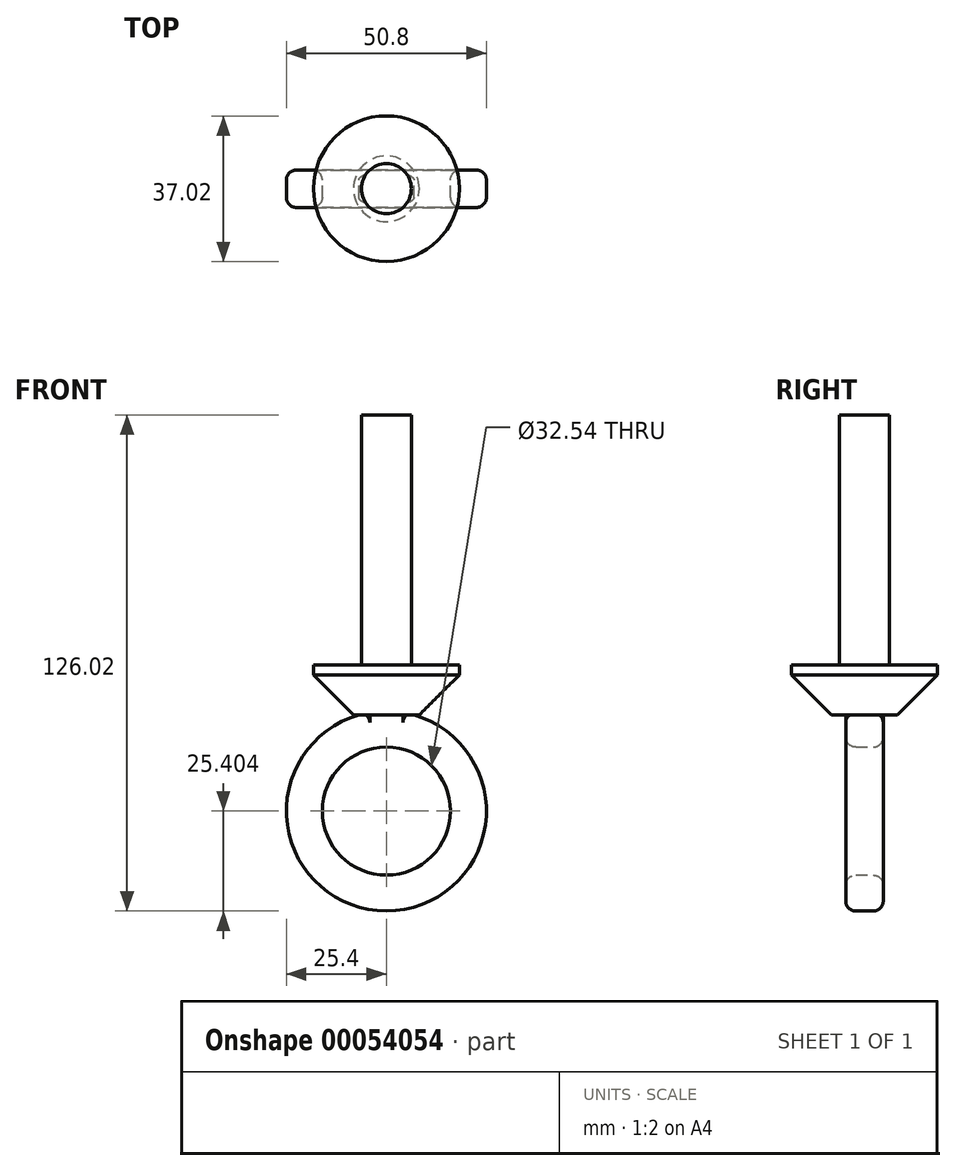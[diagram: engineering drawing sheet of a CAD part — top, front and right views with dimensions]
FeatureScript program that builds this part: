
annotation { "Feature Type Name" : "Feature", "Feature Type Description" : "" }
export const myFeature = defineFeature(function(context is Context, id is Id, definition is map)
    precondition{}
    {
        {
            var Q0;
            Q0=qCreatedBy(makeId("Top.planeOp"),FACE);
            var sketch = newSketch(context, id + "F0", { "sketchPlane" : qUnion([Q0])});
            skCircle(sketch, "E0", {"center": v(0, 0) * mm, "radius": 6.35 * mm});
            skSolve(sketch);
        }
        {
            var Q0;
            Q0=makeQuery(id+"F0.imprint","IMPRINT",FACE,{"disambiguationData":[TD([[makeQuery(id+"F0.imprint","IMPRINT",EDGE,{"derivedFrom":sQuery(id+"F0.wireOp",EDGE,"E0")}),1.0]])]});
            extrude(context, id + "F1", {"entities" : qUnion([Q0]), "depth" : 76.2 * mm});
        }
        {
            var Q0;
            Q0=qCreatedBy(makeId("Front.planeOp"),FACE);
            var sketch = newSketch(context, id + "F2", { "sketchPlane" : qUnion([Q0])});
            skCircle(sketch, "E1", {"center": v(0, -24.42) * mm, "radius": 25.4 * mm});
            skCircle(sketch, "E2", {"center": v(0, -24.42) * mm, "radius": 16.27 * mm});
            skSolve(sketch);
        }
        {
            var Q0;
            Q0=makeQuery(id+"F2.imprint","IMPRINT",FACE,{"disambiguationData":[TD([[makeQuery(id+"F2.imprint","IMPRINT",EDGE,{"derivedFrom":sQuery(id+"F2.wireOp",EDGE,"E1")}),1.0]])]});
            extrude(context, id + "F3", {"entities" : qUnion([Q0]), "operationType" : NewBodyOperationType.ADD, "depth" : 9.52 * mm, "symmetric" : true});
        }
        {
            var Q0;
            Q0=makeQuery(id+"F3.opExtrude","SWEPT_FACE",FACE,{"disambiguationData":[OSD([sQuery(id+"F2.wireOp",EDGE,"E2")])]});
            var Q1;
            Q1=makeQuery(id+"F3.opExtrude","CAP_EDGE",EDGE,{"disambiguationData":[OSD([sQuery(id+"F2.wireOp",EDGE,"E1")])],"isStart":true});
            var Q2;
            Q2=makeQuery(id+"F3.opExtrude","CAP_EDGE",EDGE,{"disambiguationData":[OSD([sQuery(id+"F2.wireOp",EDGE,"E1")])],"isStart":false});
            var Q3;
            Q3=makeQuery(id+"F3.opExtrude","CAP_EDGE",EDGE,{"disambiguationData":[OSD([sQuery(id+"F2.wireOp",EDGE,"E2")])],"isStart":false});
            fillet(context, id + "F4", {"entities" : qUnion([Q0, Q1, Q2, Q3]), "radius" : 2.54 * mm, "tangentPropagation" : true, "allowEdgeOverflow" : false});
        }
        {
            var Q0;
            Q0=qCreatedBy(makeId("Top.planeOp"),FACE);
            var sketch = newSketch(context, id + "F5", { "sketchPlane" : qUnion([Q0])});
            skCircle(sketch, "E3", {"center": v(0, 0) * mm, "radius": 18.51 * mm});
            skSolve(sketch);
        }
        {
            var Q0;
            Q0=makeQuery(id+"F5.imprint","IMPRINT",FACE,{"disambiguationData":[TD([[makeQuery(id+"F5.imprint","IMPRINT",EDGE,{"derivedFrom":sQuery(id+"F5.wireOp",EDGE,"E3")}),1.0]])]});
            extrude(context, id + "F6", {"entities" : qUnion([Q0]), "operationType" : NewBodyOperationType.ADD, "depth" : 12.7 * mm});
        }
        {
            var Q0;
            Q0=makeQuery(id+"F6.opExtrude","CAP_EDGE",EDGE,{"disambiguationData":[OSD([sQuery(id+"F5.wireOp",EDGE,"E3")])],"isStart":true});
            chamfer(context, id + "F7", {"entities" : qUnion([Q0]), "width" : 10.16 * mm, "tangentPropagation" : true});
        }
    });
